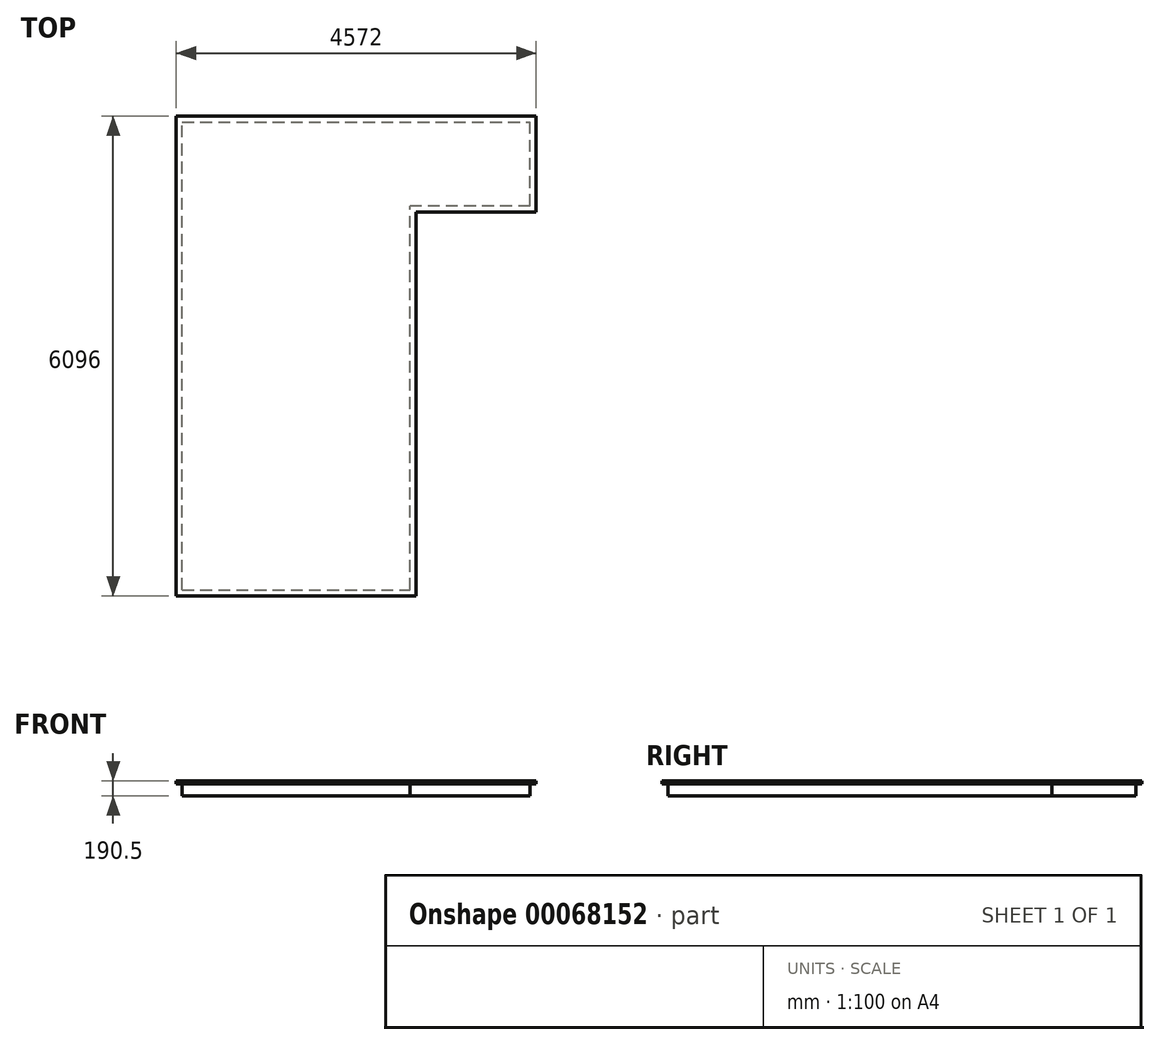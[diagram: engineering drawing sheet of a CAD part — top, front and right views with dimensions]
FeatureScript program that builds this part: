
annotation { "Feature Type Name" : "Feature", "Feature Type Description" : "" }
export const myFeature = defineFeature(function(context is Context, id is Id, definition is map)
    precondition{}
    {
        {
            var Q0;
            Q0=qCreatedBy(makeId("Top.planeOp"),FACE);
            var sketch = newSketch(context, id + "F0", { "sketchPlane" : qUnion([Q0])});
            skLineSegment(sketch, "E0.bottom", {"start": v(-1420.16, 3422.5) * mm, "end": v(3151.84, 3422.5) * mm});
            skLineSegment(sketch, "E0.top", {"start": v(-1420.16, -2673.5) * mm, "end": v(1627.84, -2673.5) * mm});
            skLineSegment(sketch, "E0.left", {"start": v(-1420.16, 3422.5) * mm, "end": v(-1420.16, -2673.5) * mm});
            skLineSegment(sketch, "E0.right", {"start": v(1627.84, 2203.3) * mm, "end": v(1627.84, -2673.5) * mm});
            skLineSegment(sketch, "E1.bottom", {"start": v(1627.84, 2203.3) * mm, "end": v(3151.84, 2203.3) * mm});
            skLineSegment(sketch, "E1.right", {"start": v(3151.84, 2203.3) * mm, "end": v(3151.84, 3422.5) * mm});
            skSolve(sketch);
        }
        {
            var Q0;
            Q0 = qSketchRegion(id + "F0", true);
            extrude(context, id + "F1", {"entities" : qUnion([Q0]), "oppositeDirection" : true, "depth" : 38.1 * mm});
        }
        {
            var Q0;
            Q0=makeQuery(id+"F1.opExtrude","CAP_FACE",FACE,{"disambiguationData":[OSD([sQuery(id+"F0.wireOp",EDGE,"E0.bottom"),sQuery(id+"F0.wireOp",EDGE,"E0.top"),sQuery(id+"F0.wireOp",EDGE,"E0.left"),sQuery(id+"F0.wireOp",EDGE,"E0.right")])],"isStart":false});
            var sketch = newSketch(context, id + "F2", { "sketchPlane" : qUnion([Q0])});
            skLineSegment(sketch, "E2.bottom", {"start": v(-1343.96, 2597.3) * mm, "end": v(1551.64, 2597.3) * mm});
            skLineSegment(sketch, "E2.top", {"start": v(-1343.96, -3346.3) * mm, "end": v(1551.64, -3346.3) * mm});
            skLineSegment(sketch, "E2.left", {"start": v(-1343.96, 2597.3) * mm, "end": v(-1343.96, -3346.3) * mm});
            skLineSegment(sketch, "E2.right", {"start": v(1551.64, 2597.3) * mm, "end": v(1551.64, -3346.3) * mm});
            skSolve(sketch);
        }
        {
            var Q0;
            Q0 = qSketchRegion(id + "F2", true);
            extrude(context, id + "F3", {"entities" : qUnion([Q0]), "operationType" : NewBodyOperationType.ADD, "depth" : 152.4 * mm});
        }
        {
            var Q0;
            Q0=makeQuery(id+"F1.opExtrude","CAP_FACE",FACE,{"disambiguationData":[OSD([sQuery(id+"F0.wireOp",EDGE,"E0.bottom"),sQuery(id+"F0.wireOp",EDGE,"E0.top"),sQuery(id+"F0.wireOp",EDGE,"E0.left"),sQuery(id+"F0.wireOp",EDGE,"E0.right"),sQuery(id+"F0.wireOp",EDGE,"E1.bottom"),sQuery(id+"F0.wireOp",EDGE,"E1.right")])],"isStart":false});
            var sketch = newSketch(context, id + "F4", { "sketchPlane" : qUnion([Q0])});
            skLineSegment(sketch, "E3.bottom", {"start": v(3075.64, -2279.5) * mm, "end": v(1551.64, -2279.5) * mm});
            skLineSegment(sketch, "E3.top", {"start": v(3075.64, -3346.3) * mm, "end": v(1551.64, -3346.3) * mm});
            skLineSegment(sketch, "E3.left", {"start": v(3075.64, -2279.5) * mm, "end": v(3075.64, -3346.3) * mm});
            skLineSegment(sketch, "E3.right", {"start": v(1551.64, -2279.5) * mm, "end": v(1551.64, -3346.3) * mm});
            skSolve(sketch);
        }
        {
            var Q0;
            Q0 = qSketchRegion(id + "F4", true);
            extrude(context, id + "F5", {"entities" : qUnion([Q0]), "operationType" : NewBodyOperationType.ADD, "depth" : 152.4 * mm});
        }
    });
